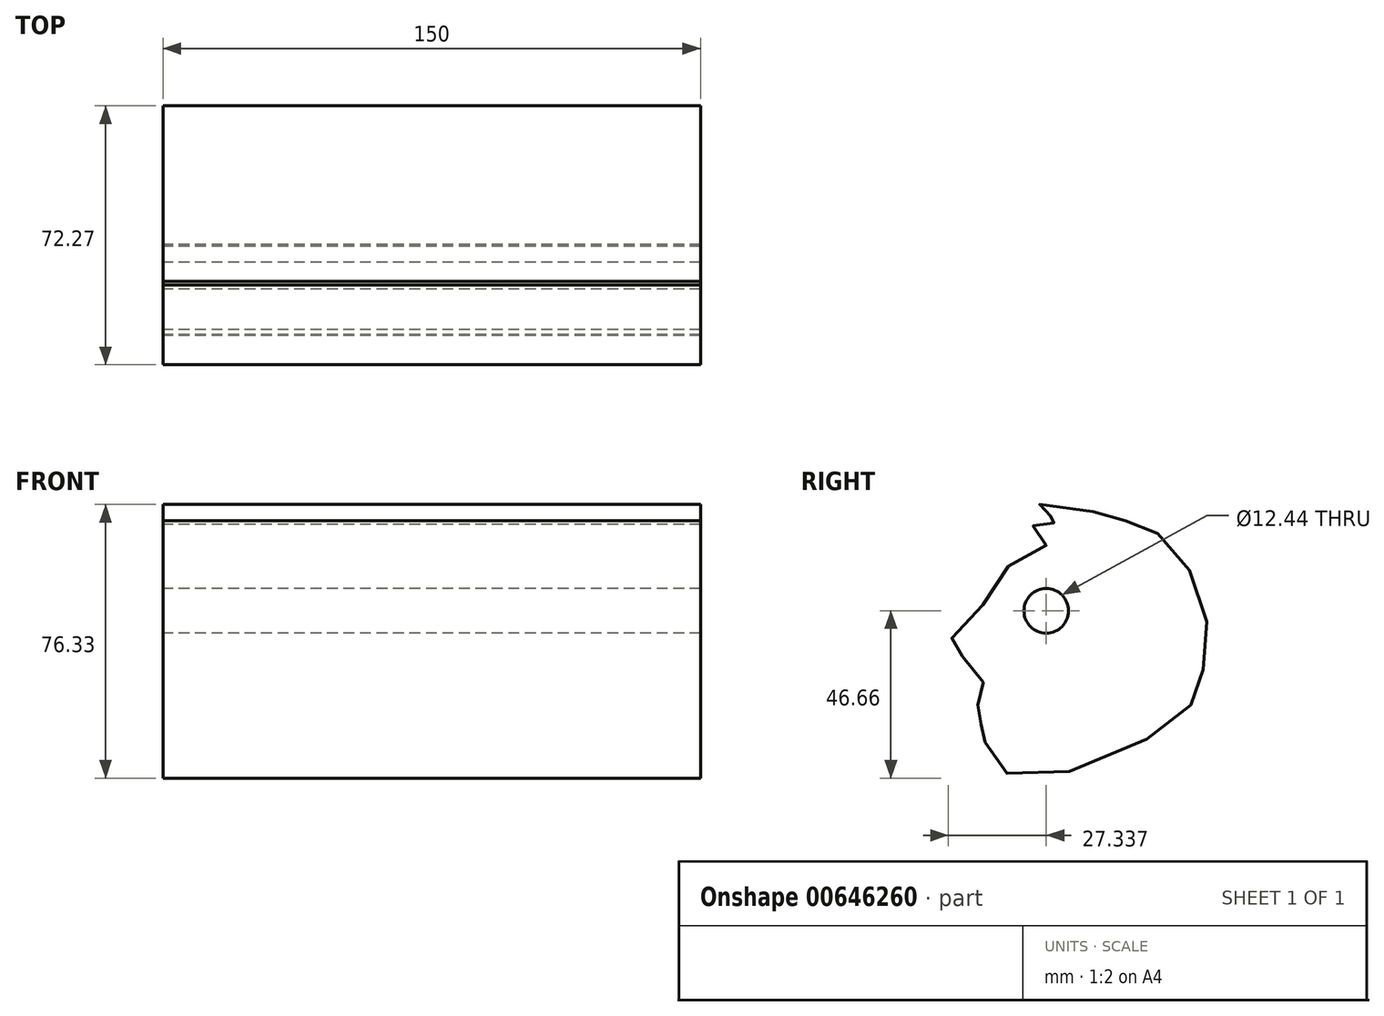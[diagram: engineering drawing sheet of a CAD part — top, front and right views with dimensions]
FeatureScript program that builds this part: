
annotation { "Feature Type Name" : "Feature", "Feature Type Description" : "" }
export const myFeature = defineFeature(function(context is Context, id is Id, definition is map)
    precondition{}
    {
        {
            var Q0;
            Q0=qCreatedBy(makeId("Right.planeOp"),FACE);
            var sketch = newSketch(context, id + "F0", { "sketchPlane" : qUnion([Q0])});
            skFitSpline(sketch, "E0", {"points": [v(-2.7, 39.9) * mm, v(-13.27, 42.76) * mm, v(-28.73, 43.72) * mm, v(-19, 38.95) * mm, v(-29.69, 39.7) * mm, v(-23.58, 34.75) * mm, v(-32.36, 29.6) * mm, v(-43.81, 14.5) * mm, v(-52.02, 4.77) * mm, v(-44.96, 0) * mm, v(-42.48, -8.02) * mm, v(-43.81, -11.65) * mm, v(-42.29, -14.7) * mm, v(-43.62, -18.52) * mm, v(-42.1, -21.38) * mm, v(-34.27, -31.3) * mm, v(10.4, -16.6) * mm, v(18.34, -4.93) * mm, v(19.57, 14.7) * mm, v(7.73, 35.32) * mm, v(-2.7, 39.9) * mm]});
            skCircle(sketch, "E1", {"center": v(-24.72, 14.7) * mm, "radius": 6.22 * mm});
            skSolve(sketch);
        }
        {
            var Q0;
            Q0=makeQuery(id+"F0.imprint","IMPRINT",FACE,{"disambiguationData":[TD([[makeQuery(id+"F0.imprint","IMPRINT",EDGE,{"derivedFrom":sQuery(id+"F0.wireOp",EDGE,"E0")}),1.0]])]});
            extrude(context, id + "F1", {"entities" : qUnion([Q0]), "endBound" : BoundingType.SYMMETRIC, "depth" : 150 * mm, "offsetDistance" : 25 * mm});
        }
    });
